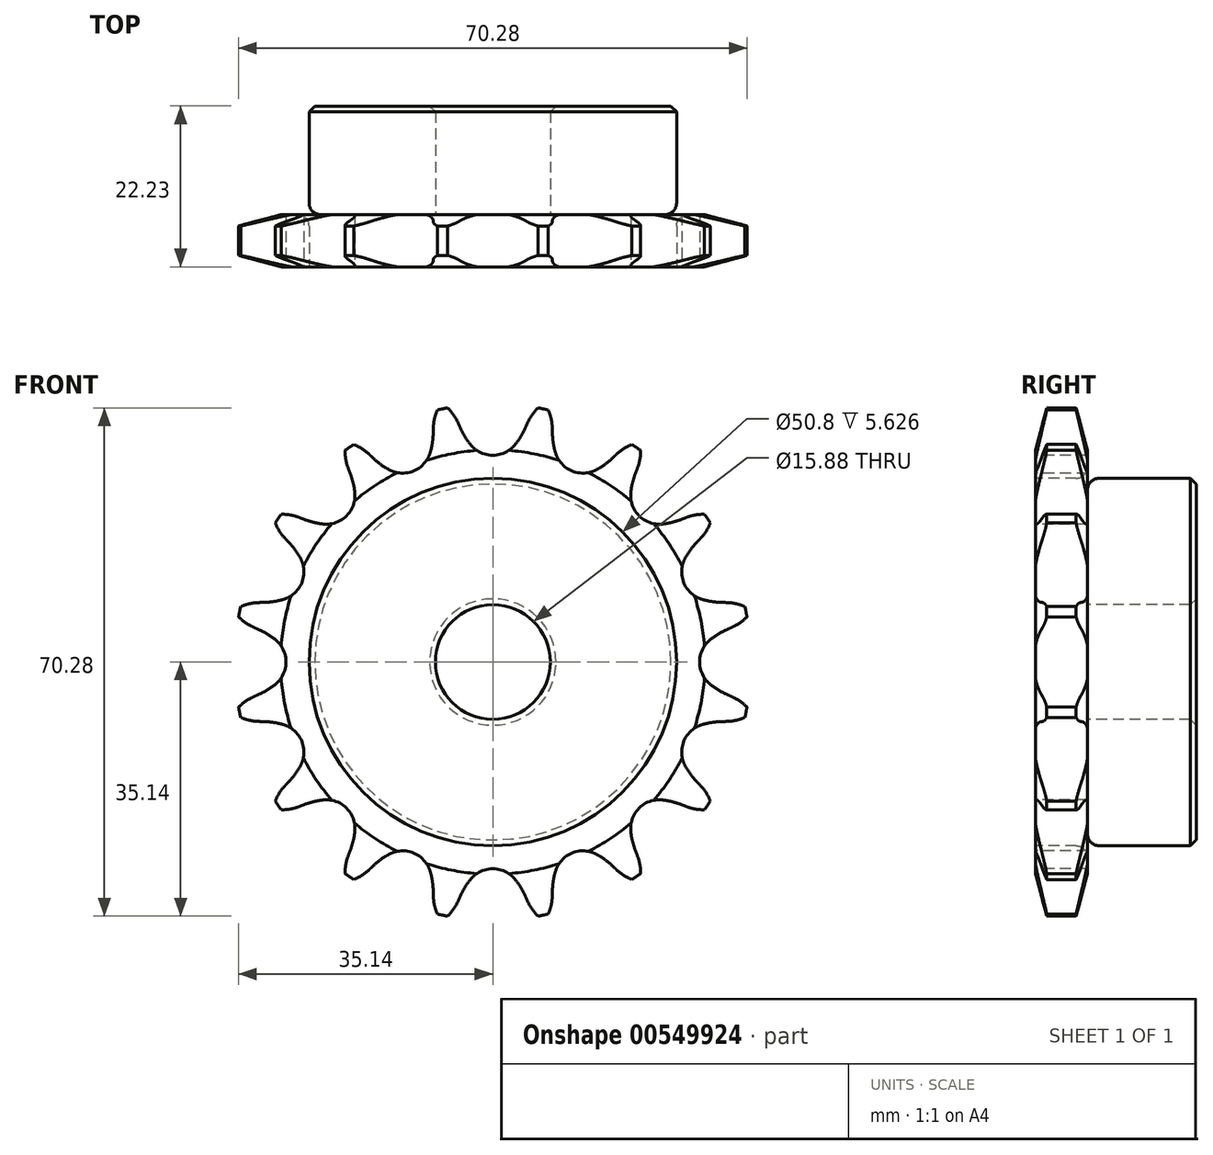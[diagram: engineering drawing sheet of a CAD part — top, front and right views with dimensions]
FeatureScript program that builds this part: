
annotation { "Feature Type Name" : "Feature", "Feature Type Description" : "" }
export const myFeature = defineFeature(function(context is Context, id is Id, definition is map)
    precondition{}
    {
        {
            var Q0;
            Q0=qCreatedBy(makeId("Right.planeOp"),FACE);
            var sketch = newSketch(context, id + "F0", { "sketchPlane" : qUnion([Q0])});
            skLineSegment(sketch, "E0", {"start": v(0, 0) * mm, "end": v(22.23, 0) * mm, "construction": true});
            skLineSegment(sketch, "E1.bottom", {"start": v(0, 7.94) * mm, "end": v(7.21, 7.94) * mm});
            skLineSegment(sketch, "E1.top", {"start": v(0, 35.69) * mm, "end": v(7.21, 35.69) * mm});
            skLineSegment(sketch, "E1.left", {"start": v(0, 7.94) * mm, "end": v(0, 35.69) * mm});
            skLineSegment(sketch, "E1.right", {"start": v(7.21, 7.94) * mm, "end": v(7.21, 35.69) * mm});
            skLineSegment(sketch, "E2.bottom", {"start": v(0, 7.94) * mm, "end": v(22.23, 7.94) * mm});
            skLineSegment(sketch, "E2.top", {"start": v(0, 25.4) * mm, "end": v(22.23, 25.4) * mm});
            skLineSegment(sketch, "E2.left", {"start": v(0, 7.94) * mm, "end": v(0, 25.4) * mm});
            skLineSegment(sketch, "E2.right", {"start": v(22.23, 7.94) * mm, "end": v(22.22, 25.4) * mm});
            skLineSegment(sketch, "E3.MirrorCS", {"start": v(0, -7.94) * mm, "end": v(7.21, -7.94) * mm});
            skLineSegment(sketch, "E4.MirrorCS", {"start": v(22.23, -7.94) * mm, "end": v(22.23, -25.4) * mm});
            skLineSegment(sketch, "E5.MirrorCS", {"start": v(0, -7.94) * mm, "end": v(0, -25.4) * mm});
            skLineSegment(sketch, "E6.MirrorCS", {"start": v(0, -35.69) * mm, "end": v(7.21, -35.69) * mm});
            skLineSegment(sketch, "E7.MirrorCS", {"start": v(0, -7.94) * mm, "end": v(0, -35.69) * mm});
            skLineSegment(sketch, "E8.MirrorCS", {"start": v(7.21, -7.94) * mm, "end": v(7.21, -35.69) * mm});
            skLineSegment(sketch, "E9.MirrorCS", {"start": v(0, -7.94) * mm, "end": v(22.23, -7.94) * mm});
            skLineSegment(sketch, "E10.MirrorCS", {"start": v(0, -25.4) * mm, "end": v(22.23, -25.4) * mm});
            skSolve(sketch);
        }
        {
            var Q0;
            {var subQ5=sQuery(id+"F0.wireOp",EDGE,"E2.left");Q0=makeQuery(id+"F0.imprint","IMPRINT",FACE,{"disambiguationData":[TD([[makeQuery(id+"F0.imprint","IMPRINT",EDGE,{"derivedFrom":subQ5}),-1.0]])]});}
            var Q1;
            {var subQ5=sQuery(id+"F0.wireOp",EDGE,"E2.right");Q1=makeQuery(id+"F0.imprint","IMPRINT",FACE,{"disambiguationData":[TD([[makeQuery(id+"F0.imprint","IMPRINT",EDGE,{"derivedFrom":subQ5}),1.0]])]});}
            var Q2;
            {var subQ0=sQuery(id+"F0.wireOp",EDGE,"E1.top");Q2=makeQuery(id+"F0.imprint","IMPRINT",FACE,{"disambiguationData":[TD([[makeQuery(id+"F0.imprint","IMPRINT",EDGE,{"derivedFrom":subQ0}),-1.0]])]});}
            var Q3;
            Q3=sQuery(id+"F0.wireOp",EDGE,"E0");
            revolve(context, id + "F1", {"entities" : qUnion([Q0, Q1, Q2]), "axis" : qUnion([Q3]), "revolveType" : RevolveType.FULL});
        }
        {
            var Q0;
            Q0=makeQuery(id+"F1.opRevolve","SWEPT_EDGE",EDGE,{"disambiguationData":[OSD([sQuery(id+"F0.wireOp",EDGE,"E1.right"),sQuery(id+"F0.wireOp",EDGE,"E2.top")])]});
            fillet(context, id + "F2", {"entities" : qUnion([Q0]), "radius" : 1.59 * mm, "tangentPropagation" : true, "allowEdgeOverflow" : false});
        }
        {
            var Q0;
            Q0=makeQuery(id+"F1.opRevolve","SWEPT_FACE",FACE,{"disambiguationData":[OSD([sQuery(id+"F0.wireOp",EDGE,"E2.right")])]});
            chamfer(context, id + "F3", {"entities" : qUnion([Q0]), "width" : 0.8 * mm, "tangentPropagation" : true});
        }
        {
            var Q0;
            Q0=makeQuery(id+"F1.opRevolve","SWEPT_FACE",FACE,{"disambiguationData":[OSD([sQuery(id+"F0.wireOp",EDGE,"E1.top")])]});
            chamfer(context, id + "F4", {"entities" : qUnion([Q0]), "chamferType" : ChamferType.TWO_OFFSETS, "width1" : 6.35 * mm, "oppositeDirection" : false, "width2" : 1.57 * mm, "tangentPropagation" : true});
        }
        {
            var Q0;
            Q0=makeQuery(id+"F1.opRevolve","SWEPT_FACE",FACE,{"disambiguationData":[OSD([sQuery(id+"F0.wireOp",EDGE,"E1.left"),sQuery(id+"F0.wireOp",EDGE,"E2.left")])]});
            var sketch = newSketch(context, id + "F5", { "sketchPlane" : qUnion([Q0])});
            skCircle(sketch, "E11", {"center": v(0, 0) * mm, "radius": 32.55 * mm, "construction": true});
            skLineSegment(sketch, "E12", {"start": v(0, 0) * mm, "end": v(0, 32.55) * mm, "construction": true});
            skLineSegment(sketch, "E13", {"start": v(0, 32.55) * mm, "end": v(41.42, 32.55) * mm, "construction": true});
            skLineSegment(sketch, "E14", {"start": v(0, 32.55) * mm, "end": v(5, 36.56) * mm});
            skLineSegment(sketch, "E15", {"start": v(5, 36.56) * mm, "end": v(-4.46, 32.3) * mm});
            skLineSegment(sketch, "E16", {"start": v(-4.46, 32.3) * mm, "end": v(-4.82, 33.1) * mm});
            skLineSegment(sketch, "E17", {"start": v(0, 0) * mm, "end": v(-7.13, 35.85) * mm, "construction": true});
            skArc(sketch, "E18", {"start": v(-7.13, 35.85) * mm, "mid": v(-15.87, 26.15) * mm, "end": v(-4.82, 33.1) * mm, "construction": true});
            skArc(sketch, "E19", {"start": v(-4.82, 33.1) * mm, "mid": v(-5.78, 34.63) * mm, "end": v(-7.13, 35.85) * mm});
            skArc(sketch, "E20", {"start": v(-4.46, 32.3) * mm, "mid": v(-3.84, 31.14) * mm, "end": v(-3.1, 30.07) * mm});
            skArc(sketch, "E21.MirrorCS", {"start": v(-4.46, 32.3) * mm, "mid": v(-4, 31.07) * mm, "end": v(-3.7, 29.8) * mm});
            skArc(sketch, "E22.MirrorCS", {"start": v(4.82, 33.1) * mm, "mid": v(5.78, 34.63) * mm, "end": v(7.13, 35.85) * mm});
            skLineSegment(sketch, "E23.MirrorCS", {"start": v(4.46, 32.3) * mm, "end": v(4.82, 33.1) * mm});
            skArc(sketch, "E24.MirrorCS", {"start": v(4.46, 32.3) * mm, "mid": v(3.84, 31.14) * mm, "end": v(3.1, 30.07) * mm});
            skArc(sketch, "E25", {"start": v(-3.1, 30.07) * mm, "mid": v(0, 28.59) * mm, "end": v(3.1, 30.07) * mm});
            skArc(sketch, "E26", {"start": v(3.1, 30.07) * mm, "mid": v(0, 36.51) * mm, "end": v(-3.1, 30.07) * mm, "construction": true});
            skLineSegment(sketch, "E27.1.0", {"start": v(-25.74, -20) * mm, "end": v(-26.26, -20.72) * mm});
            skArc(sketch, "E27.1.1", {"start": v(-25.74, -20) * mm, "mid": v(-25.05, -18.9) * mm, "end": v(-24.5, -17.71) * mm});
            skArc(sketch, "E27.1.2", {"start": v(-24.5, -17.71) * mm, "mid": v(-24.76, -14.3) * mm, "end": v(-27.59, -12.36) * mm});
            skArc(sketch, "E27.1.3", {"start": v(-30.2, -12.3) * mm, "mid": v(-28.9, -12.24) * mm, "end": v(-27.59, -12.36) * mm});
            skLineSegment(sketch, "E27.1.4", {"start": v(-30.2, -12.3) * mm, "end": v(-31.07, -12.38) * mm});
            skArc(sketch, "E27.1.5", {"start": v(-31.07, -12.38) * mm, "mid": v(-32.89, -12.3) * mm, "end": v(-34.61, -11.75) * mm});
            skArc(sketch, "E27.1.6", {"start": v(-26.26, -20.72) * mm, "mid": v(-27.1, -22.33) * mm, "end": v(-27.48, -24.1) * mm});
            skLineSegment(sketch, "E27.2.0", {"start": v(30.2, -12.3) * mm, "end": v(31.07, -12.38) * mm});
            skArc(sketch, "E27.2.1", {"start": v(30.2, -12.3) * mm, "mid": v(28.9, -12.24) * mm, "end": v(27.59, -12.36) * mm});
            skArc(sketch, "E27.2.2", {"start": v(27.59, -12.36) * mm, "mid": v(24.76, -14.3) * mm, "end": v(24.5, -17.71) * mm});
            skArc(sketch, "E27.2.3", {"start": v(25.74, -20) * mm, "mid": v(25.05, -18.9) * mm, "end": v(24.5, -17.71) * mm});
            skLineSegment(sketch, "E27.2.4", {"start": v(25.74, -20) * mm, "end": v(26.26, -20.72) * mm});
            skArc(sketch, "E27.2.5", {"start": v(26.26, -20.72) * mm, "mid": v(27.1, -22.33) * mm, "end": v(27.48, -24.1) * mm});
            skArc(sketch, "E27.2.6", {"start": v(31.07, -12.38) * mm, "mid": v(32.89, -12.3) * mm, "end": v(34.61, -11.75) * mm});
            skArc(sketch, "E28.1.0", {"start": v(-17.12, 28.74) * mm, "mid": v(-18.6, 29.79) * mm, "end": v(-20.3, 30.4) * mm});
            skLineSegment(sketch, "E28.1.1", {"start": v(-16.48, 28.14) * mm, "end": v(-17.12, 28.74) * mm});
            skArc(sketch, "E28.1.2", {"start": v(-16.48, 28.14) * mm, "mid": v(-15.47, 27.3) * mm, "end": v(-14.36, 26.6) * mm});
            skArc(sketch, "E28.1.3", {"start": v(-14.36, 26.6) * mm, "mid": v(-10.94, 26.41) * mm, "end": v(-8.65, 28.96) * mm});
            skArc(sketch, "E28.1.4", {"start": v(-8.24, 31.55) * mm, "mid": v(-8.37, 30.24) * mm, "end": v(-8.65, 28.96) * mm});
            skLineSegment(sketch, "E28.1.5", {"start": v(-8.24, 31.55) * mm, "end": v(-8.22, 32.42) * mm});
            skArc(sketch, "E28.1.6", {"start": v(-8.22, 32.42) * mm, "mid": v(-7.91, 34.21) * mm, "end": v(-7.13, 35.85) * mm});
            skArc(sketch, "E28.2.0", {"start": v(-26.8, 20) * mm, "mid": v(-28.58, 20.4) * mm, "end": v(-30.4, 20.3) * mm});
            skLineSegment(sketch, "E28.2.1", {"start": v(-26, 19.69) * mm, "end": v(-26.8, 20) * mm});
            skArc(sketch, "E28.2.2", {"start": v(-26, 19.69) * mm, "mid": v(-24.74, 19.3) * mm, "end": v(-23.45, 19.08) * mm});
            skArc(sketch, "E28.2.3", {"start": v(-23.45, 19.08) * mm, "mid": v(-20.21, 20.21) * mm, "end": v(-19.08, 23.45) * mm});
            skArc(sketch, "E28.2.4", {"start": v(-19.69, 26) * mm, "mid": v(-19.3, 24.74) * mm, "end": v(-19.08, 23.45) * mm});
            skLineSegment(sketch, "E28.2.5", {"start": v(-19.69, 26) * mm, "end": v(-20, 26.8) * mm});
            skArc(sketch, "E28.2.6", {"start": v(-20, 26.8) * mm, "mid": v(-20.4, 28.58) * mm, "end": v(-20.3, 30.4) * mm});
            skArc(sketch, "E28.3.0", {"start": v(-32.42, 8.22) * mm, "mid": v(-34.21, 7.91) * mm, "end": v(-35.85, 7.13) * mm});
            skLineSegment(sketch, "E28.3.1", {"start": v(-31.55, 8.24) * mm, "end": v(-32.42, 8.22) * mm});
            skArc(sketch, "E28.3.2", {"start": v(-31.55, 8.24) * mm, "mid": v(-30.24, 8.37) * mm, "end": v(-28.96, 8.65) * mm});
            skArc(sketch, "E28.3.3", {"start": v(-28.96, 8.65) * mm, "mid": v(-26.41, 10.94) * mm, "end": v(-26.6, 14.36) * mm});
            skArc(sketch, "E28.3.4", {"start": v(-28.14, 16.48) * mm, "mid": v(-27.3, 15.47) * mm, "end": v(-26.6, 14.36) * mm});
            skLineSegment(sketch, "E28.3.5", {"start": v(-28.14, 16.48) * mm, "end": v(-28.74, 17.12) * mm});
            skArc(sketch, "E28.3.6", {"start": v(-28.74, 17.12) * mm, "mid": v(-29.79, 18.6) * mm, "end": v(-30.4, 20.3) * mm});
            skArc(sketch, "E28.4.0", {"start": v(-33.1, -4.82) * mm, "mid": v(-34.63, -5.78) * mm, "end": v(-35.85, -7.13) * mm});
            skLineSegment(sketch, "E28.4.1", {"start": v(-32.3, -4.46) * mm, "end": v(-33.1, -4.82) * mm});
            skArc(sketch, "E28.4.2", {"start": v(-32.3, -4.46) * mm, "mid": v(-31.14, -3.84) * mm, "end": v(-30.07, -3.1) * mm});
            skArc(sketch, "E28.4.3", {"start": v(-30.07, -3.1) * mm, "mid": v(-28.59, 0) * mm, "end": v(-30.07, 3.1) * mm});
            skArc(sketch, "E28.4.4", {"start": v(-32.3, 4.46) * mm, "mid": v(-31.14, 3.84) * mm, "end": v(-30.07, 3.1) * mm});
            skLineSegment(sketch, "E28.4.5", {"start": v(-32.3, 4.46) * mm, "end": v(-33.1, 4.82) * mm});
            skArc(sketch, "E28.4.6", {"start": v(-33.1, 4.82) * mm, "mid": v(-34.63, 5.78) * mm, "end": v(-35.85, 7.13) * mm});
            skArc(sketch, "E28.5.0", {"start": v(-28.74, -17.12) * mm, "mid": v(-29.79, -18.6) * mm, "end": v(-30.4, -20.3) * mm});
            skLineSegment(sketch, "E28.5.1", {"start": v(-28.14, -16.48) * mm, "end": v(-28.74, -17.12) * mm});
            skArc(sketch, "E28.5.2", {"start": v(-28.14, -16.48) * mm, "mid": v(-27.3, -15.47) * mm, "end": v(-26.6, -14.36) * mm});
            skArc(sketch, "E28.5.3", {"start": v(-26.6, -14.36) * mm, "mid": v(-26.41, -10.94) * mm, "end": v(-28.96, -8.65) * mm});
            skArc(sketch, "E28.5.4", {"start": v(-31.55, -8.24) * mm, "mid": v(-30.24, -8.37) * mm, "end": v(-28.96, -8.65) * mm});
            skLineSegment(sketch, "E28.5.5", {"start": v(-31.55, -8.24) * mm, "end": v(-32.42, -8.22) * mm});
            skArc(sketch, "E28.5.6", {"start": v(-32.42, -8.22) * mm, "mid": v(-34.21, -7.91) * mm, "end": v(-35.85, -7.13) * mm});
            skArc(sketch, "E28.6.0", {"start": v(-20, -26.8) * mm, "mid": v(-20.4, -28.58) * mm, "end": v(-20.3, -30.4) * mm});
            skLineSegment(sketch, "E28.6.1", {"start": v(-19.69, -26) * mm, "end": v(-20, -26.8) * mm});
            skArc(sketch, "E28.6.2", {"start": v(-19.69, -26) * mm, "mid": v(-19.3, -24.74) * mm, "end": v(-19.08, -23.45) * mm});
            skArc(sketch, "E28.6.3", {"start": v(-19.08, -23.45) * mm, "mid": v(-20.21, -20.21) * mm, "end": v(-23.45, -19.08) * mm});
            skArc(sketch, "E28.6.4", {"start": v(-26, -19.69) * mm, "mid": v(-24.74, -19.3) * mm, "end": v(-23.45, -19.08) * mm});
            skLineSegment(sketch, "E28.6.5", {"start": v(-26, -19.69) * mm, "end": v(-26.8, -20) * mm});
            skArc(sketch, "E28.6.6", {"start": v(-26.8, -20) * mm, "mid": v(-28.58, -20.4) * mm, "end": v(-30.4, -20.3) * mm});
            skArc(sketch, "E28.7.0", {"start": v(-8.22, -32.42) * mm, "mid": v(-7.91, -34.21) * mm, "end": v(-7.13, -35.85) * mm});
            skLineSegment(sketch, "E28.7.1", {"start": v(-8.24, -31.55) * mm, "end": v(-8.22, -32.42) * mm});
            skArc(sketch, "E28.7.2", {"start": v(-8.24, -31.55) * mm, "mid": v(-8.37, -30.24) * mm, "end": v(-8.65, -28.96) * mm});
            skArc(sketch, "E28.7.3", {"start": v(-8.65, -28.96) * mm, "mid": v(-10.94, -26.41) * mm, "end": v(-14.36, -26.6) * mm});
            skArc(sketch, "E28.7.4", {"start": v(-16.48, -28.14) * mm, "mid": v(-15.47, -27.3) * mm, "end": v(-14.36, -26.6) * mm});
            skLineSegment(sketch, "E28.7.5", {"start": v(-16.48, -28.14) * mm, "end": v(-17.12, -28.74) * mm});
            skArc(sketch, "E28.7.6", {"start": v(-17.12, -28.74) * mm, "mid": v(-18.6, -29.79) * mm, "end": v(-20.3, -30.4) * mm});
            skArc(sketch, "E28.8.0", {"start": v(4.82, -33.1) * mm, "mid": v(5.78, -34.63) * mm, "end": v(7.13, -35.85) * mm});
            skLineSegment(sketch, "E28.8.1", {"start": v(4.46, -32.3) * mm, "end": v(4.82, -33.1) * mm});
            skArc(sketch, "E28.8.2", {"start": v(4.46, -32.3) * mm, "mid": v(3.84, -31.14) * mm, "end": v(3.1, -30.07) * mm});
            skArc(sketch, "E28.8.3", {"start": v(3.1, -30.07) * mm, "mid": v(0, -28.59) * mm, "end": v(-3.1, -30.07) * mm});
            skArc(sketch, "E28.8.4", {"start": v(-4.46, -32.3) * mm, "mid": v(-3.84, -31.14) * mm, "end": v(-3.1, -30.07) * mm});
            skLineSegment(sketch, "E28.8.5", {"start": v(-4.46, -32.3) * mm, "end": v(-4.82, -33.1) * mm});
            skArc(sketch, "E28.8.6", {"start": v(-4.82, -33.1) * mm, "mid": v(-5.78, -34.63) * mm, "end": v(-7.13, -35.85) * mm});
            skArc(sketch, "E28.9.0", {"start": v(17.12, -28.74) * mm, "mid": v(18.6, -29.79) * mm, "end": v(20.3, -30.4) * mm});
            skLineSegment(sketch, "E28.9.1", {"start": v(16.48, -28.14) * mm, "end": v(17.12, -28.74) * mm});
            skArc(sketch, "E28.9.2", {"start": v(16.48, -28.14) * mm, "mid": v(15.47, -27.3) * mm, "end": v(14.36, -26.6) * mm});
            skArc(sketch, "E28.9.3", {"start": v(14.36, -26.6) * mm, "mid": v(10.94, -26.41) * mm, "end": v(8.65, -28.96) * mm});
            skArc(sketch, "E28.9.4", {"start": v(8.24, -31.55) * mm, "mid": v(8.37, -30.24) * mm, "end": v(8.65, -28.96) * mm});
            skLineSegment(sketch, "E28.9.5", {"start": v(8.24, -31.55) * mm, "end": v(8.22, -32.42) * mm});
            skArc(sketch, "E28.9.6", {"start": v(8.22, -32.42) * mm, "mid": v(7.91, -34.21) * mm, "end": v(7.13, -35.85) * mm});
            skArc(sketch, "E28.10.0", {"start": v(26.8, -20) * mm, "mid": v(28.58, -20.4) * mm, "end": v(30.4, -20.3) * mm});
            skLineSegment(sketch, "E28.10.1", {"start": v(26, -19.69) * mm, "end": v(26.8, -20) * mm});
            skArc(sketch, "E28.10.2", {"start": v(26, -19.69) * mm, "mid": v(24.74, -19.3) * mm, "end": v(23.45, -19.08) * mm});
            skArc(sketch, "E28.10.3", {"start": v(23.45, -19.08) * mm, "mid": v(20.21, -20.21) * mm, "end": v(19.08, -23.45) * mm});
            skArc(sketch, "E28.10.4", {"start": v(19.69, -26) * mm, "mid": v(19.3, -24.74) * mm, "end": v(19.08, -23.45) * mm});
            skLineSegment(sketch, "E28.10.5", {"start": v(19.69, -26) * mm, "end": v(20, -26.8) * mm});
            skArc(sketch, "E28.10.6", {"start": v(20, -26.8) * mm, "mid": v(20.4, -28.58) * mm, "end": v(20.3, -30.4) * mm});
            skArc(sketch, "E28.11.0", {"start": v(32.42, -8.22) * mm, "mid": v(34.21, -7.91) * mm, "end": v(35.85, -7.13) * mm});
            skLineSegment(sketch, "E28.11.1", {"start": v(31.55, -8.24) * mm, "end": v(32.42, -8.22) * mm});
            skArc(sketch, "E28.11.2", {"start": v(31.55, -8.24) * mm, "mid": v(30.24, -8.37) * mm, "end": v(28.96, -8.65) * mm});
            skArc(sketch, "E28.11.3", {"start": v(28.96, -8.65) * mm, "mid": v(26.41, -10.94) * mm, "end": v(26.6, -14.36) * mm});
            skArc(sketch, "E28.11.4", {"start": v(28.14, -16.48) * mm, "mid": v(27.3, -15.47) * mm, "end": v(26.6, -14.36) * mm});
            skLineSegment(sketch, "E28.11.5", {"start": v(28.14, -16.48) * mm, "end": v(28.74, -17.12) * mm});
            skArc(sketch, "E28.11.6", {"start": v(28.74, -17.12) * mm, "mid": v(29.79, -18.6) * mm, "end": v(30.4, -20.3) * mm});
            skArc(sketch, "E28.12.0", {"start": v(33.1, 4.82) * mm, "mid": v(34.63, 5.78) * mm, "end": v(35.85, 7.13) * mm});
            skLineSegment(sketch, "E28.12.1", {"start": v(32.3, 4.46) * mm, "end": v(33.1, 4.82) * mm});
            skArc(sketch, "E28.12.2", {"start": v(32.3, 4.46) * mm, "mid": v(31.14, 3.84) * mm, "end": v(30.07, 3.1) * mm});
            skArc(sketch, "E28.12.3", {"start": v(30.07, 3.1) * mm, "mid": v(28.59, 0) * mm, "end": v(30.07, -3.1) * mm});
            skArc(sketch, "E28.12.4", {"start": v(32.3, -4.46) * mm, "mid": v(31.14, -3.84) * mm, "end": v(30.07, -3.1) * mm});
            skLineSegment(sketch, "E28.12.5", {"start": v(32.3, -4.46) * mm, "end": v(33.1, -4.82) * mm});
            skArc(sketch, "E28.12.6", {"start": v(33.1, -4.82) * mm, "mid": v(34.63, -5.78) * mm, "end": v(35.85, -7.13) * mm});
            skArc(sketch, "E28.13.0", {"start": v(28.74, 17.12) * mm, "mid": v(29.79, 18.6) * mm, "end": v(30.4, 20.3) * mm});
            skLineSegment(sketch, "E28.13.1", {"start": v(28.14, 16.48) * mm, "end": v(28.74, 17.12) * mm});
            skArc(sketch, "E28.13.2", {"start": v(28.14, 16.48) * mm, "mid": v(27.3, 15.47) * mm, "end": v(26.6, 14.36) * mm});
            skArc(sketch, "E28.13.3", {"start": v(26.6, 14.36) * mm, "mid": v(26.41, 10.94) * mm, "end": v(28.96, 8.65) * mm});
            skArc(sketch, "E28.13.4", {"start": v(31.55, 8.24) * mm, "mid": v(30.24, 8.37) * mm, "end": v(28.96, 8.65) * mm});
            skLineSegment(sketch, "E28.13.5", {"start": v(31.55, 8.24) * mm, "end": v(32.42, 8.22) * mm});
            skArc(sketch, "E28.13.6", {"start": v(32.42, 8.22) * mm, "mid": v(34.21, 7.91) * mm, "end": v(35.85, 7.13) * mm});
            skArc(sketch, "E28.14.0", {"start": v(20, 26.8) * mm, "mid": v(20.4, 28.58) * mm, "end": v(20.3, 30.4) * mm});
            skLineSegment(sketch, "E28.14.1", {"start": v(19.69, 26) * mm, "end": v(20, 26.8) * mm});
            skArc(sketch, "E28.14.2", {"start": v(19.69, 26) * mm, "mid": v(19.3, 24.74) * mm, "end": v(19.08, 23.45) * mm});
            skArc(sketch, "E28.14.3", {"start": v(19.08, 23.45) * mm, "mid": v(20.21, 20.21) * mm, "end": v(23.45, 19.08) * mm});
            skArc(sketch, "E28.14.4", {"start": v(26, 19.69) * mm, "mid": v(24.74, 19.3) * mm, "end": v(23.45, 19.08) * mm});
            skLineSegment(sketch, "E28.14.5", {"start": v(26, 19.69) * mm, "end": v(26.8, 20) * mm});
            skArc(sketch, "E28.14.6", {"start": v(26.8, 20) * mm, "mid": v(28.58, 20.4) * mm, "end": v(30.4, 20.3) * mm});
            skArc(sketch, "E28.15.0", {"start": v(8.22, 32.42) * mm, "mid": v(7.91, 34.21) * mm, "end": v(7.13, 35.85) * mm});
            skLineSegment(sketch, "E28.15.1", {"start": v(8.24, 31.55) * mm, "end": v(8.22, 32.42) * mm});
            skArc(sketch, "E28.15.2", {"start": v(8.24, 31.55) * mm, "mid": v(8.37, 30.24) * mm, "end": v(8.65, 28.96) * mm});
            skArc(sketch, "E28.15.3", {"start": v(8.65, 28.96) * mm, "mid": v(10.94, 26.41) * mm, "end": v(14.36, 26.6) * mm});
            skArc(sketch, "E28.15.4", {"start": v(16.48, 28.14) * mm, "mid": v(15.47, 27.3) * mm, "end": v(14.36, 26.6) * mm});
            skLineSegment(sketch, "E28.15.5", {"start": v(16.48, 28.14) * mm, "end": v(17.12, 28.74) * mm});
            skArc(sketch, "E28.15.6", {"start": v(17.12, 28.74) * mm, "mid": v(18.6, 29.79) * mm, "end": v(20.3, 30.4) * mm});
            skSolve(sketch);
        }
        {
            var Q0;
            Q0 = qSketchRegion(id + "F5", true);
            extrude(context, id + "F6", {"entities" : qUnion([Q0]), "operationType" : NewBodyOperationType.INTERSECT, "endBound" : BoundingType.THROUGH_ALL, "oppositeDirection" : true, "depth" : 31.5 * mm, "offsetDistance" : 25.4 * mm});
        }
    });
